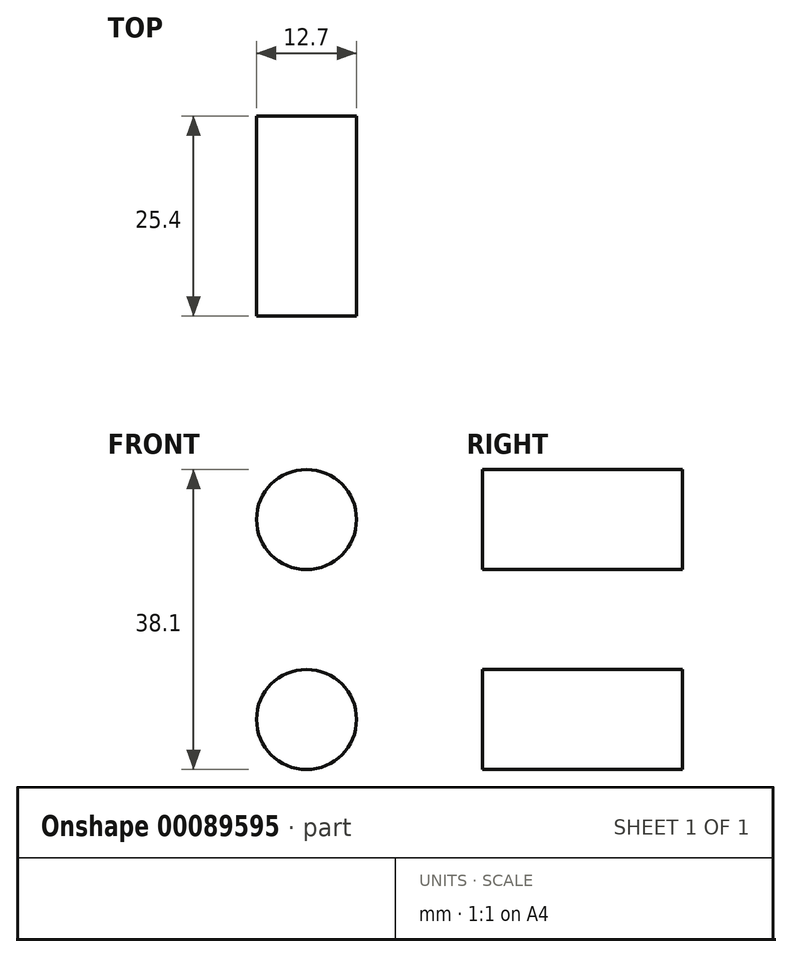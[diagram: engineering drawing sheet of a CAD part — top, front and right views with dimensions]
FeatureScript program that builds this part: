
annotation { "Feature Type Name" : "Feature", "Feature Type Description" : "" }
export const myFeature = defineFeature(function(context is Context, id is Id, definition is map)
    precondition{}
    {
        {
            var Q0;
            Q0=qCreatedBy(makeId("Front.planeOp"),FACE);
            var sketch = newSketch(context, id + "F0", { "sketchPlane" : qUnion([Q0])});
            skLineSegment(sketch, "E0", {"start": v(-50.8, 25.4) * mm, "end": v(50.8, 25.4) * mm});
            skLineSegment(sketch, "E1", {"start": v(50.8, 25.4) * mm, "end": v(50.8, -25.4) * mm});
            skLineSegment(sketch, "E2", {"start": v(50.8, -25.4) * mm, "end": v(-50.8, -25.4) * mm});
            skLineSegment(sketch, "E3", {"start": v(-50.8, -25.4) * mm, "end": v(-50.8, 25.4) * mm});
            skSolve(sketch);
        }
        {
            var Q0;
            Q0=makeQuery(id+"F0.imprint","IMPRINT",FACE,{"disambiguationData":[TD([[makeQuery(id+"F0.imprint","IMPRINT",EDGE,{"derivedFrom":sQuery(id+"F0.wireOp",EDGE,"E0")}),-1.0]])]});
            extrude(context, id + "F1", {"entities" : qUnion([Q0]), "depth" : 25.4 * mm});
        }
        {
            var Q0;
            Q0=makeQuery(id+"F1.opExtrude","CAP_FACE",FACE,{"disambiguationData":[OSD([sQuery(id+"F0.wireOp",EDGE,"E0"),sQuery(id+"F0.wireOp",EDGE,"E1"),sQuery(id+"F0.wireOp",EDGE,"E2"),sQuery(id+"F0.wireOp",EDGE,"E3")])],"isStart":false});
            var sketch = newSketch(context, id + "F2", { "sketchPlane" : qUnion([Q0])});
            skCircle(sketch, "E4", {"center": v(-38.1, 12.7) * mm, "radius": 6.35 * mm});
            skCircle(sketch, "E5", {"center": v(-38.1, -12.7) * mm, "radius": 6.35 * mm});
            skCircle(sketch, "E6.MirrorC", {"center": v(38.1, -12.7) * mm, "radius": 6.35 * mm});
            skCircle(sketch, "E7.MirrorC", {"center": v(38.1, 12.7) * mm, "radius": 6.35 * mm});
            skSolve(sketch);
        }
        {
            var Q0;
            Q0=makeQuery(id+"F2.imprint","IMPRINT",FACE,{"disambiguationData":[TD([[makeQuery(id+"F2.imprint","IMPRINT",EDGE,{"derivedFrom":sQuery(id+"F2.wireOp",EDGE,"E4")}),1.0]])]});
            var Q1;
            Q1=makeQuery(id+"F2.imprint","IMPRINT",FACE,{"disambiguationData":[TD([[makeQuery(id+"F2.imprint","IMPRINT",EDGE,{"derivedFrom":sQuery(id+"F2.wireOp",EDGE,"E5")}),1.0]])]});
            var Q2;
            Q2=makeQuery(id+"F2.imprint","IMPRINT",FACE,{"disambiguationData":[TD([[makeQuery(id+"F2.imprint","IMPRINT",EDGE,{"derivedFrom":sQuery(id+"F2.wireOp",EDGE,"E6.MirrorC")}),-1.0]])]});
            var Q3;
            Q3=makeQuery(id+"F2.imprint","IMPRINT",FACE,{"disambiguationData":[TD([[makeQuery(id+"F2.imprint","IMPRINT",EDGE,{"derivedFrom":sQuery(id+"F2.wireOp",EDGE,"E7.MirrorC")}),-1.0]])]});
            extrude(context, id + "F3", {"entities" : qUnion([Q0, Q1, Q2, Q3]), "operationType" : NewBodyOperationType.REMOVE, "oppositeDirection" : true, "depth" : 25.4 * mm});
        }
    });
